# Revit family: Alcon-13340-MD-M-Revit-Family
name_source: partatom
category: Generic Models
units: mm (PartAtom-declared; Revit-internal decimal feet)

## family parameters
Can host rebar = No
Cut with Voids When Loaded = No
Host = Face
Maintain Annotation Orientation = No
Part Type = Normal
Room Calculation Point = No
Round Connector Dimension = Use Diameter
Shared = No

## types (6) — shared parameters
Default Elevation = 4' - 0"
Fixture Rotation = 90.00°
Housing = Housing
Manufacturer = Alcon Ligthing
Product Page = https://www.alconlighting.com
URL = https://www.alconlighting.com

## per-type parameters (varying)
| type | Louver | Model | Snoot |
| Round Canopy | No | 13340-SM-M | No |
| Square Canopy | No | 13340-SM-M | No |
| Round Canopy and Louver | Yes | 13340-SM-M | No |
| Round Canopy and Snoot | No | 13340-SM-M | Yes |
| Square Canopy and Louver | Yes | 13340-SM-M | No |
| Square Canopy and Snoot | No | 13340-MD-M | Yes |

type visibility flags (boolean, named after types; folded from table):
- Round Canopy: Yes: Round Canopy
- Square Canopy: Yes: Square Canopy
- Round Canopy and Louver: Yes: Round Canopy
- Round Canopy and Snoot: Yes: Round Canopy
- Square Canopy and Louver: Yes: Square Canopy
- Square Canopy and Snoot: Yes: Square Canopy

## geometry (parser evidence)
native form markers: Sweep x10
no freeform markers — native parametric forms only
